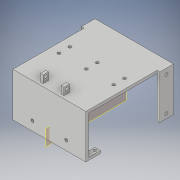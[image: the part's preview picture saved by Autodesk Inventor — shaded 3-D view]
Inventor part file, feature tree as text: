
AUTODESK INVENTOR PART (.ipt)
format: ipt  version: 2018 (Build 220112000, 112)  size: 331,776 bytes
history: native  units: mm
features: extrude x10, sketch x9, other x7, projected_geometry x3, plane x2, mirror x1
ambient origin geometry x8: Origin, YZ Plane, XZ Plane, XY Plane, X Axis, Y Axis, Z Axis, Center Point
bodies: Solid1 (feature_tree)
feature tree (32):
  other  "Wheel Base.ipt"
  extrude  "Extrusion1"  Depth=6.0mm
  extrude  "Extrusion2"  Depth=3.0mm
  extrude  "Extrusion3"  Depth=3.0mm
  extrude  "Extrusion4"  Depth=90.0mm
  extrude  "Extrusion5"  Depth=80.0mm
  extrude  "Extrusion6"  Depth=10.0mm
  extrude  "Extrusion7"  Depth=6.0mm
  extrude  "Extrusion8"  Depth=20.0mm
  extrude  "Extrusion9"  Depth=8.0mm TaperAngle=0.0deg
  extrude  "Extrusion10"  Depth=3.0mm
  mirror  "Mirror1"
  other  "TaggingFeature1"
  plane  "Work Plane1"
  sketch  "Sketch3"  dims[d0=10.0mm d2=6.0mm]
  sketch  "Sketch4"  dims[d4=3.0mm d5=0.0mm d6=3.0mm]
  sketch  "Sketch5"  dims[d7=45.0mm d8=0.0mm d9=3.0mm]
  sketch  "Sketch6"  dims[d10=90.0mm d11=0.0mm d12=3.2mm]
  projected_geometry  "Projected Loop1"
  sketch  "Sketch7"  dims[d13=37.0mm d14=80.0mm]
  projected_geometry  "Projected Loop2"
  other  "TaggingFeature2"
  plane  "Work Plane1_1"
  sketch  "Sketch9"  dims[d15=21.5mm d16=10.0mm]
  sketch  "Sketch11"  dims[d17=80.0mm d18=0.0mm d19=6.0mm]
  projected_geometry  "Projected Loop3"
  sketch  "Sketch12"  dims[d20=3.0mm d21=20.0mm]
  sketch  "Sketch13"  dims[d22=3.0mm d23=8.0mm d24=0.0mm d25=3.2mm d26=6.0mm d27=0.0mm d28=10.0mm d29=10.0mm d30=3.2mm d32=12.0mm d33=30.0mm d34=30.0mm d35=10.0mm d36=80.0mm d37=93.0mm d38=40.5mm d39=6.0mm d40=0.0mm d43=15.0mm d44=3.2mm d45=37.0mm d46=48.0mm d47=6.0mm d48=3.0mm d49=0.0mm d50=6.0mm d51=3.0mm d52=6.0mm d53=0.0mm d54=6.0mm d55=0.0mm d56=3.0mm]
  other  "Solid1::Wheel Base.ipt"
  other  "Srf1"
  other  "Solid1::Wheel Base.ipt_1"
  other  "Srf2"
